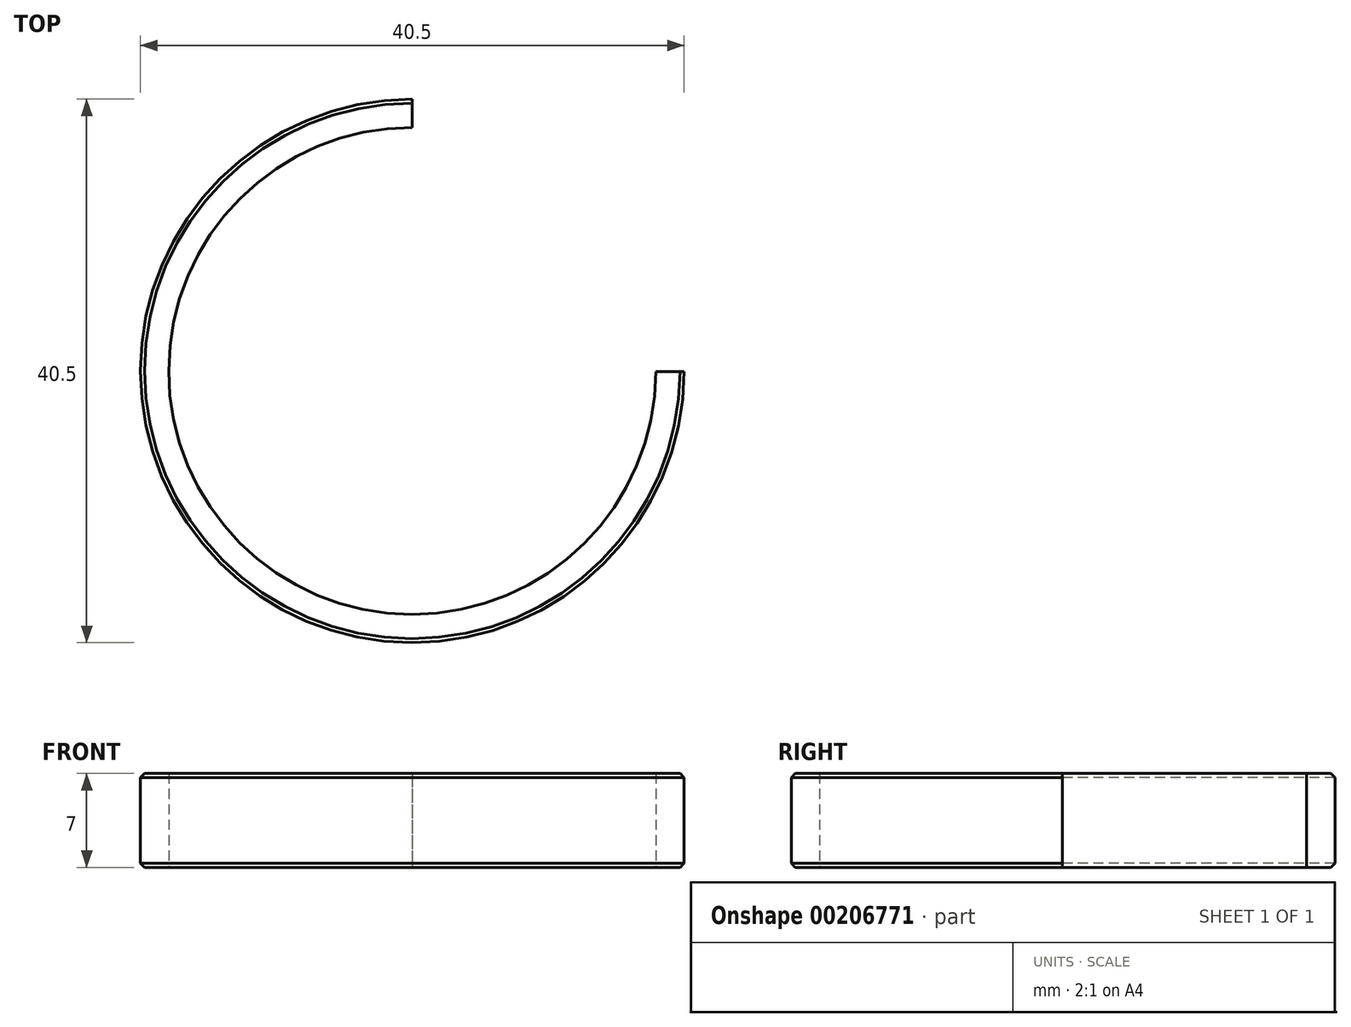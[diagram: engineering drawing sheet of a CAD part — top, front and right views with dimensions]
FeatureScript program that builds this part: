
annotation { "Feature Type Name" : "Feature", "Feature Type Description" : "" }
export const myFeature = defineFeature(function(context is Context, id is Id, definition is map)
    precondition{}
    {
        {
            var Q0;
            Q0=qCreatedBy(makeId("Top.planeOp"),FACE);
            var sketch = newSketch(context, id + "F0", { "sketchPlane" : qUnion([Q0])});
            skCircle(sketch, "E0", {"center": v(0, 0) * mm, "radius": 18.15 * mm});
            skCircle(sketch, "E1", {"center": v(0, 0) * mm, "radius": 20.25 * mm});
            skLineSegment(sketch, "E2", {"start": v(0, 0) * mm, "end": v(0, 48.58) * mm});
            skLineSegment(sketch, "E3", {"start": v(0, 0) * mm, "end": v(52.47, -0.13) * mm});
            skLineSegment(sketch, "E4", {"start": v(0, 18.15) * mm, "end": v(18.15, -0.05) * mm});
            skSolve(sketch);
        }
        {
            var Q0;
            {var subQ0=sQuery(id+"F0.wireOp",EDGE,"E2");var subQ1=sQuery(id+"F0.wireOp",EDGE,"E0");var subQ2=makeQuery(id+"F0.imprint","INTERSECT",VERTEX,{"derivedFrom":[subQ1,subQ0]});Q0=makeQuery(id+"F0.imprint","IMPRINT",FACE,{"disambiguationData":[TD([[makeQuery(id+"F0.imprint","IMPRINT",EDGE,{"disambiguationData":[TD([[subQ2,-1.0]])],"derivedFrom":subQ1}),-1.0]])]});}
            extrude(context, id + "F1", {"entities" : qUnion([Q0]), "depth" : 7 * mm});
        }
        {
            var Q0;
            Q0=makeQuery(id+"F1.opExtrude","CAP_EDGE",EDGE,{"disambiguationData":[OSD([sQuery(id+"F0.wireOp",EDGE,"E1")])],"isStart":false});
            var Q1;
            Q1=makeQuery(id+"F1.opExtrude","CAP_EDGE",EDGE,{"disambiguationData":[OSD([sQuery(id+"F0.wireOp",EDGE,"E1")])],"isStart":true});
            chamfer(context, id + "F2", {"entities" : qUnion([Q0, Q1]), "width" : .3 * mm, "tangentPropagation" : true});
        }
    });
